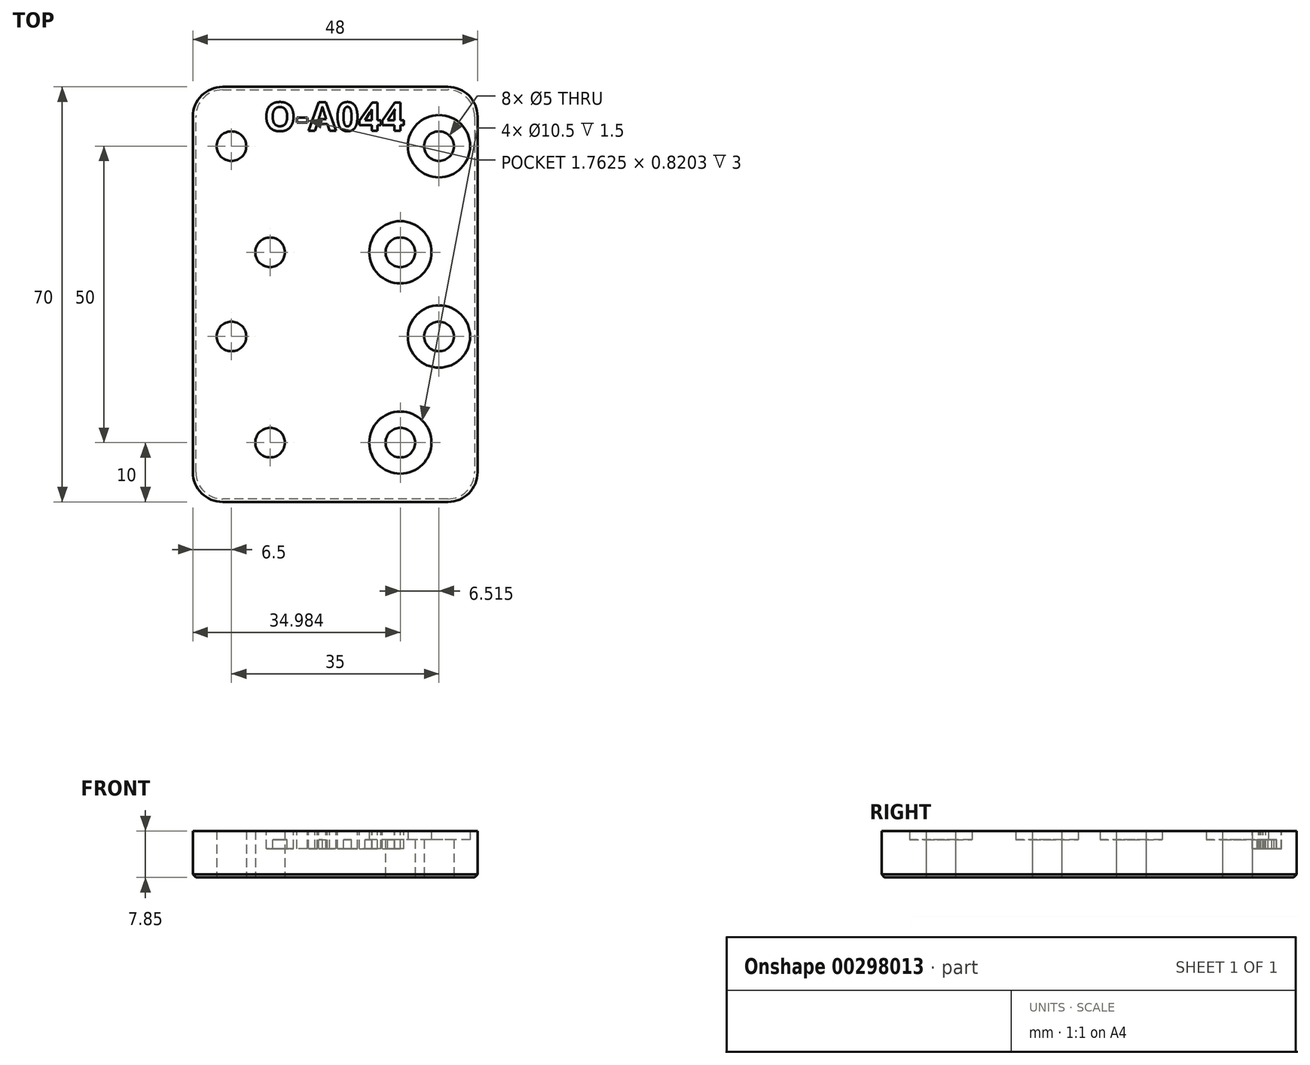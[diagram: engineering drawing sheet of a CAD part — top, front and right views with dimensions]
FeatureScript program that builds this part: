
annotation { "Feature Type Name" : "Feature", "Feature Type Description" : "" }
export const myFeature = defineFeature(function(context is Context, id is Id, definition is map)
    precondition{}
    {
        {
            var Q0;
            Q0=qCreatedBy(makeId("Top.planeOp"),FACE);
            var sketch = newSketch(context, id + "F0", { "sketchPlane" : qUnion([Q0])});
            skLineSegment(sketch, "E0.bottom", {"start": v(-24, 35) * mm, "end": v(24, 35) * mm});
            skLineSegment(sketch, "E0.top", {"start": v(-24, -35) * mm, "end": v(24, -35) * mm});
            skLineSegment(sketch, "E0.left", {"start": v(-24, 35) * mm, "end": v(-24, -35) * mm});
            skLineSegment(sketch, "E0.right", {"start": v(24, 35) * mm, "end": v(24, -35) * mm});
            skPoint(sketch, "E0.middle", {"position": v(0, 0) * mm});
            skCircle(sketch, "E1", {"center": v(-10.98, 7.1) * mm, "radius": 2.5 * mm});
            skCircle(sketch, "E2", {"center": v(-17.5, 25) * mm, "radius": 2.5 * mm});
            skLineSegment(sketch, "E3", {"start": v(-17.5, 25) * mm, "end": v(-10.98, 7.1) * mm, "construction": true});
            skCircle(sketch, "E4", {"center": v(-10.98, -25) * mm, "radius": 2.5 * mm});
            skCircle(sketch, "E5", {"center": v(-17.5, -7.1) * mm, "radius": 2.5 * mm});
            skLineSegment(sketch, "E6", {"start": v(-17.5, -7.1) * mm, "end": v(0, -7.1) * mm, "construction": true});
            skLineSegment(sketch, "E7", {"start": v(-17.5, -7.1) * mm, "end": v(-10.98, -25) * mm, "construction": true});
            skLineSegment(sketch, "E8", {"start": v(-17.5, 25) * mm, "end": v(-24, 25) * mm, "construction": true});
            skCircle(sketch, "E9.MirrorC", {"center": v(17.5, 25) * mm, "radius": 2.5 * mm});
            skCircle(sketch, "E10.MirrorC", {"center": v(10.98, 7.1) * mm, "radius": 2.5 * mm});
            skCircle(sketch, "E11.MirrorC", {"center": v(17.5, -7.1) * mm, "radius": 2.5 * mm});
            skCircle(sketch, "E12.MirrorC", {"center": v(10.98, -25) * mm, "radius": 2.5 * mm});
            skSolve(sketch);
        }
        {
            var Q0;
            Q0=makeQuery(id+"F0.imprint","IMPRINT",FACE,{"disambiguationData":[TD([[makeQuery(id+"F0.imprint","IMPRINT",EDGE,{"derivedFrom":sQuery(id+"F0.wireOp",EDGE,"E0.bottom")}),-1.0]])]});
            extrude(context, id + "F1", {"entities" : qUnion([Q0]), "depth" : 6.35 * mm});
        }
        {
            var Q0;
            Q0=makeQuery(id+"F1.opExtrude","SWEPT_EDGE",EDGE,{"disambiguationData":[OSD([sQuery(id+"F0.wireOp",EDGE,"E0.bottom"),sQuery(id+"F0.wireOp",EDGE,"E0.left")])]});
            var Q1;
            Q1=makeQuery(id+"F1.opExtrude","SWEPT_EDGE",EDGE,{"disambiguationData":[OSD([sQuery(id+"F0.wireOp",EDGE,"E0.bottom"),sQuery(id+"F0.wireOp",EDGE,"E0.right")])]});
            var Q2;
            Q2=makeQuery(id+"F1.opExtrude","SWEPT_EDGE",EDGE,{"disambiguationData":[OSD([sQuery(id+"F0.wireOp",EDGE,"E0.top"),sQuery(id+"F0.wireOp",EDGE,"E0.left")])]});
            var Q3;
            Q3=makeQuery(id+"F1.opExtrude","SWEPT_EDGE",EDGE,{"disambiguationData":[OSD([sQuery(id+"F0.wireOp",EDGE,"E0.top"),sQuery(id+"F0.wireOp",EDGE,"E0.right")])]});
            fillet(context, id + "F2", {"entities" : qUnion([Q0, Q1, Q2, Q3]), "radius" : 5 * mm, "tangentPropagation" : true, "allowEdgeOverflow" : false});
        }
        {
            var Q0;
            Q0=makeQuery(id+"F1.opExtrude","CAP_FACE",FACE,{"disambiguationData":[OSD([sQuery(id+"F0.wireOp",EDGE,"E0.bottom"),sQuery(id+"F0.wireOp",EDGE,"E0.top"),sQuery(id+"F0.wireOp",EDGE,"E0.left"),sQuery(id+"F0.wireOp",EDGE,"E0.right"),sQuery(id+"F0.wireOp",EDGE,"E1"),sQuery(id+"F0.wireOp",EDGE,"E2"),sQuery(id+"F0.wireOp",EDGE,"E4"),sQuery(id+"F0.wireOp",EDGE,"E5"),sQuery(id+"F0.wireOp",EDGE,"E9.MirrorC"),sQuery(id+"F0.wireOp",EDGE,"E10.MirrorC"),sQuery(id+"F0.wireOp",EDGE,"E11.MirrorC"),sQuery(id+"F0.wireOp",EDGE,"E12.MirrorC")])],"isStart":false});
            var sketch = newSketch(context, id + "F3", { "sketchPlane" : qUnion([Q0])});
            skText(sketch, "E13", { "text": "O-A044", "fontName": "OpenSans-Bold.ttf"});
            skPoint(sketch, "E14", {"position": v(0, 30) * mm});
            const initialGuessF3  = {"E13": [-0.012, 0.02758, 1, 0, 0.00484]};
            skSetInitialGuess(sketch, initialGuessF3);
            skSolve(sketch);
        }
        {
            var Q0;
            Q0 = qSketchRegion(id + "F3", true);
            extrude(context, id + "F4", {"entities" : qUnion([Q0]), "operationType" : NewBodyOperationType.REMOVE, "oppositeDirection" : true, "depth" : 1.5 * mm});
        }
        {
            var Q0;
            Q0=makeQuery(id+"F1.opExtrude","CAP_EDGE",EDGE,{"disambiguationData":[OSD([sQuery(id+"F0.wireOp",EDGE,"E0.top")])],"isStart":true});
            chamfer(context, id + "F5", {"entities" : qUnion([Q0]), "width" : 0.5 * mm, "tangentPropagation" : true});
        }
        {
            var Q0;
            {var subQ0=sQuery(id+"F0.wireOp",EDGE,"E0.right");var subQ1=sQuery(id+"F0.wireOp",EDGE,"E0.bottom");var subQ2=sQuery(id+"F0.wireOp",EDGE,"E2");var subQ3=sQuery(id+"F0.wireOp",EDGE,"E0.left");var subQ4=sQuery(id+"F0.wireOp",EDGE,"E1");var subQ5=sQuery(id+"F0.wireOp",EDGE,"E4");var subQ6=sQuery(id+"F0.wireOp",EDGE,"E0.top");var subQ7=sQuery(id+"F0.wireOp",EDGE,"E5");var subQ8=sQuery(id+"F0.wireOp",EDGE,"E9.MirrorC");var subQ9=sQuery(id+"F0.wireOp",EDGE,"E10.MirrorC");var subQ10=sQuery(id+"F0.wireOp",EDGE,"E11.MirrorC");var subQ11=sQuery(id+"F0.wireOp",EDGE,"E12.MirrorC");Q0=makeQuery(id+"F4.boolean.opBoolean","SPLIT",FACE,{"disambiguationData":[TD([makeQuery(id+"F1.opExtrude","SWEPT_FACE",FACE,{"disambiguationData":[OSD([subQ1])]})])],"derivedFrom":makeQuery(id+"F1.opExtrude","CAP_FACE",FACE,{"disambiguationData":[OSD([subQ1,subQ6,subQ3,subQ0,subQ4,subQ2,subQ5,subQ7,subQ8,subQ9,subQ10,subQ11])],"isStart":false})});}
            var sketch = newSketch(context, id + "F6", { "sketchPlane" : qUnion([Q0])});
            skCircle(sketch, "E15.0", {"center": v(-17.5, 25) * mm, "radius": 2.5 * mm});
            skCircle(sketch, "E16.0", {"center": v(-10.98, 7.1) * mm, "radius": 2.5 * mm});
            skCircle(sketch, "E17.0", {"center": v(-17.5, -7.1) * mm, "radius": 2.5 * mm});
            skCircle(sketch, "E18.0", {"center": v(-10.98, -25) * mm, "radius": 2.5 * mm});
            skCircle(sketch, "E19", {"center": v(-17.5, 25) * mm, "radius": 5.25 * mm});
            skCircle(sketch, "E20", {"center": v(-10.98, 7.1) * mm, "radius": 5.25 * mm});
            skCircle(sketch, "E21", {"center": v(-17.5, -7.1) * mm, "radius": 5.25 * mm});
            skCircle(sketch, "E22", {"center": v(-10.98, -25) * mm, "radius": 5.25 * mm});
            skCircle(sketch, "E23.MirrorC", {"center": v(17.5, 25) * mm, "radius": 5.25 * mm});
            skCircle(sketch, "E24.MirrorC", {"center": v(10.98, 7.1) * mm, "radius": 5.25 * mm});
            skCircle(sketch, "E25.MirrorC", {"center": v(17.5, -7.1) * mm, "radius": 5.25 * mm});
            skCircle(sketch, "E26.MirrorC", {"center": v(10.98, 7.1) * mm, "radius": 2.5 * mm});
            skCircle(sketch, "E27.MirrorC", {"center": v(17.5, 25) * mm, "radius": 2.5 * mm});
            skCircle(sketch, "E28.MirrorC", {"center": v(17.5, -7.1) * mm, "radius": 2.5 * mm});
            skCircle(sketch, "E29.MirrorC", {"center": v(10.98, -25) * mm, "radius": 5.25 * mm});
            skCircle(sketch, "E30.MirrorC", {"center": v(10.98, -25) * mm, "radius": 2.5 * mm});
            skSolve(sketch);
        }
        {
            var Q0;
            Q0=makeQuery(id+"F6.imprint","IMPRINT",FACE,{"disambiguationData":[TD([[makeQuery(id+"F6.imprint","IMPRINT",EDGE,{"derivedFrom":sQuery(id+"F6.wireOp",EDGE,"E15.0")}),-1.0]])]});
            var Q1;
            Q1=makeQuery(id+"F6.imprint","IMPRINT",FACE,{"disambiguationData":[TD([[makeQuery(id+"F6.imprint","IMPRINT",EDGE,{"derivedFrom":sQuery(id+"F6.wireOp",EDGE,"E16.0")}),-1.0]])]});
            var Q2;
            Q2=makeQuery(id+"F6.imprint","IMPRINT",FACE,{"disambiguationData":[TD([[makeQuery(id+"F6.imprint","IMPRINT",EDGE,{"derivedFrom":sQuery(id+"F6.wireOp",EDGE,"E23.MirrorC")}),-1.0]])]});
            var Q3;
            Q3=makeQuery(id+"F6.imprint","IMPRINT",FACE,{"disambiguationData":[TD([[makeQuery(id+"F6.imprint","IMPRINT",EDGE,{"derivedFrom":sQuery(id+"F6.wireOp",EDGE,"E24.MirrorC")}),-1.0]])]});
            var Q4;
            Q4=makeQuery(id+"F6.imprint","IMPRINT",FACE,{"disambiguationData":[TD([[makeQuery(id+"F6.imprint","IMPRINT",EDGE,{"derivedFrom":sQuery(id+"F6.wireOp",EDGE,"E25.MirrorC")}),-1.0]])]});
            var Q5;
            Q5=makeQuery(id+"F6.imprint","IMPRINT",FACE,{"disambiguationData":[TD([[makeQuery(id+"F6.imprint","IMPRINT",EDGE,{"derivedFrom":sQuery(id+"F6.wireOp",EDGE,"E29.MirrorC")}),-1.0]])]});
            var Q6;
            Q6=makeQuery(id+"F6.imprint","IMPRINT",FACE,{"disambiguationData":[TD([[makeQuery(id+"F6.imprint","IMPRINT",EDGE,{"derivedFrom":sQuery(id+"F6.wireOp",EDGE,"E18.0")}),-1.0]])]});
            var Q7;
            Q7=makeQuery(id+"F6.imprint","IMPRINT",FACE,{"disambiguationData":[TD([[makeQuery(id+"F6.imprint","IMPRINT",EDGE,{"derivedFrom":sQuery(id+"F6.wireOp",EDGE,"E17.0")}),-1.0]])]});
            extrude(context, id + "F7", {"entities" : qUnion([Q0, Q1, Q2, Q3, Q4, Q5, Q6, Q7]), "operationType" : NewBodyOperationType.ADD, "depth" : 1.5 * mm});
        }
    });
